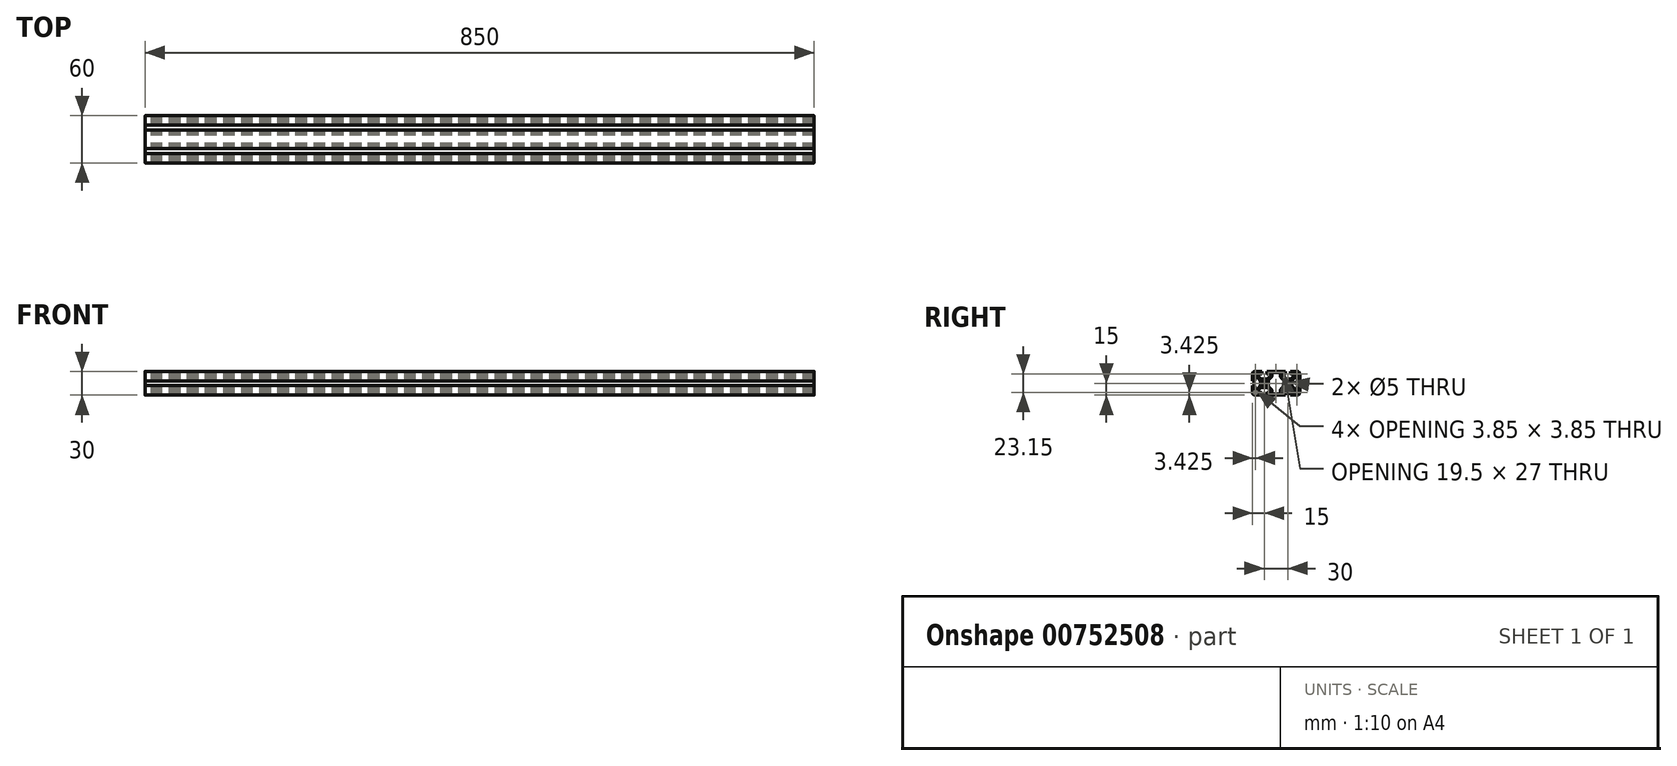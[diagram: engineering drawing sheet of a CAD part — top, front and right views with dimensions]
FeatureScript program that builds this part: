
annotation { "Feature Type Name" : "Feature", "Feature Type Description" : "" }
export const myFeature = defineFeature(function(context is Context, id is Id, definition is map)
    precondition{}
    {
        {
            var Q0;
            Q0=qCreatedBy(makeId("Right.planeOp"),FACE);
            var sketch = newSketch(context, id + "F0", { "sketchPlane" : qUnion([Q0])});
            skLineSegment(sketch, "E0.bottom", {"start": v(-12, 15) * mm, "end": v(-3.1, 15) * mm});
            skLineSegment(sketch, "E0.top", {"start": v(-12, -15) * mm, "end": v(-3.1, -15) * mm});
            skLineSegment(sketch, "E1", {"start": v(0, 31.7) * mm, "end": v(0, -24.01) * mm, "construction": true});
            skLineSegment(sketch, "E2", {"start": v(-29.71, 0) * mm, "end": v(21.95, 0) * mm, "construction": true});
            skLineSegment(sketch, "E3", {"start": v(-3.1, 15) * mm, "end": v(-3.1, 12.8) * mm});
            skLineSegment(sketch, "E4", {"start": v(-3.9, 12) * mm, "end": v(-5.6, 12) * mm});
            skLineSegment(sketch, "E5", {"start": v(-5.6, 12) * mm, "end": v(-5.6, 13.5) * mm});
            skLineSegment(sketch, "E6", {"start": v(-5.6, 13.5) * mm, "end": v(-8.15, 13.5) * mm});
            skLineSegment(sketch, "E7", {"start": v(-8.15, 13.5) * mm, "end": v(-8.15, 10.8) * mm});
            skLineSegment(sketch, "E8", {"start": v(-7.27, 8.68) * mm, "end": v(-4.72, 6.13) * mm});
            skLineSegment(sketch, "E9", {"start": v(-2.6, 5.25) * mm, "end": v(2.6, 5.25) * mm});
            skLineSegment(sketch, "E10", {"start": v(4.72, 6.13) * mm, "end": v(7.27, 8.68) * mm});
            skLineSegment(sketch, "E11", {"start": v(8.15, 10.8) * mm, "end": v(8.15, 13.5) * mm});
            skLineSegment(sketch, "E12", {"start": v(8.15, 13.5) * mm, "end": v(5.6, 13.5) * mm});
            skLineSegment(sketch, "E13", {"start": v(5.6, 13.5) * mm, "end": v(5.6, 12) * mm});
            skLineSegment(sketch, "E14", {"start": v(5.6, 12) * mm, "end": v(3.9, 12) * mm});
            skLineSegment(sketch, "E15", {"start": v(3.1, 12.8) * mm, "end": v(3.1, 15) * mm});
            skLineSegment(sketch, "E16.trimOffspring", {"start": v(3.1, 15) * mm, "end": v(12, 15) * mm});
            skLineSegment(sketch, "E17.bottom", {"start": v(-12, 13.5) * mm, "end": v(-9.65, 13.5) * mm});
            skLineSegment(sketch, "E17.top", {"start": v(-13.5, 9.65) * mm, "end": v(-9.65, 9.65) * mm});
            skLineSegment(sketch, "E17.left", {"start": v(-13.5, 12) * mm, "end": v(-13.5, 9.65) * mm});
            skLineSegment(sketch, "E17.right", {"start": v(-9.65, 13.5) * mm, "end": v(-9.65, 9.65) * mm});
            skPoint(sketch, "E18.visualSharp", {"position": v(-13.5, 13.5) * mm});
            skArc(sketch, "E18.filletArc", {"start": v(-12, 13.5) * mm, "mid": v(-13.06, 13.06) * mm, "end": v(-13.5, 12) * mm});
            skPoint(sketch, "E19.visualSharp", {"position": v(-14.85, 15) * mm});
            skArc(sketch, "E19.filletArc", {"start": v(-12, 15) * mm, "mid": v(-14.12, 14.12) * mm, "end": v(-15, 12) * mm});
            skPoint(sketch, "E20.visualSharp", {"position": v(-14.85, -15) * mm});
            skArc(sketch, "E20.filletArc", {"start": v(-15, -12) * mm, "mid": v(-14.12, -14.12) * mm, "end": v(-12, -15) * mm});
            skPoint(sketch, "E21.visualSharp", {"position": v(15.15, -15) * mm});
            skPoint(sketch, "E22.visualSharp", {"position": v(-8.15, 9.56) * mm});
            skArc(sketch, "E22.filletArc", {"start": v(-8.15, 10.8) * mm, "mid": v(-7.92, 9.66) * mm, "end": v(-7.27, 8.68) * mm});
            skPoint(sketch, "E23.visualSharp", {"position": v(-3.84, 5.25) * mm});
            skArc(sketch, "E23.filletArc", {"start": v(-4.72, 6.13) * mm, "mid": v(-3.74, 5.48) * mm, "end": v(-2.6, 5.25) * mm});
            skPoint(sketch, "E24.visualSharp", {"position": v(3.84, 5.25) * mm});
            skArc(sketch, "E24.filletArc", {"start": v(2.6, 5.25) * mm, "mid": v(3.74, 5.48) * mm, "end": v(4.72, 6.13) * mm});
            skPoint(sketch, "E25.visualSharp", {"position": v(8.15, 9.56) * mm});
            skArc(sketch, "E25.filletArc", {"start": v(7.27, 8.68) * mm, "mid": v(7.92, 9.66) * mm, "end": v(8.15, 10.8) * mm});
            skPoint(sketch, "E26.visualSharp", {"position": v(3.1, 12) * mm});
            skArc(sketch, "E26.filletArc", {"start": v(3.1, 12.8) * mm, "mid": v(3.33, 12.23) * mm, "end": v(3.9, 12) * mm});
            skPoint(sketch, "E27.visualSharp", {"position": v(-3.1, 12) * mm});
            skArc(sketch, "E27.filletArc", {"start": v(-3.9, 12) * mm, "mid": v(-3.33, 12.23) * mm, "end": v(-3.1, 12.8) * mm});
            skLineSegment(sketch, "E28.1.0", {"start": v(-5.25, -2.6) * mm, "end": v(-5.25, 2.6) * mm});
            skLineSegment(sketch, "E28.1.1", {"start": v(-12.8, 3.1) * mm, "end": v(-15, 3.1) * mm});
            skLineSegment(sketch, "E28.1.2", {"start": v(-6.13, 4.72) * mm, "end": v(-8.68, 7.27) * mm});
            skPoint(sketch, "E28.1.3", {"position": v(-12, -3.1) * mm});
            skLineSegment(sketch, "E28.1.4", {"start": v(-13.5, -5.6) * mm, "end": v(-13.5, -8.15) * mm});
            skPoint(sketch, "E28.1.5", {"position": v(-5.25, 3.84) * mm});
            skLineSegment(sketch, "E28.1.6", {"start": v(-13.5, -12) * mm, "end": v(-13.5, -9.65) * mm});
            skPoint(sketch, "E28.1.7", {"position": v(-5.25, -3.84) * mm});
            skLineSegment(sketch, "E28.1.8", {"start": v(-10.8, 8.15) * mm, "end": v(-13.5, 8.15) * mm});
            skLineSegment(sketch, "E28.1.9", {"start": v(-9.65, -13.5) * mm, "end": v(-9.65, -9.65) * mm});
            skLineSegment(sketch, "E28.1.10", {"start": v(-12, -13.5) * mm, "end": v(-9.65, -13.5) * mm});
            skLineSegment(sketch, "E28.1.11", {"start": v(-13.5, -8.15) * mm, "end": v(-10.8, -8.15) * mm});
            skLineSegment(sketch, "E28.1.12", {"start": v(-13.5, -9.65) * mm, "end": v(-9.65, -9.65) * mm});
            skPoint(sketch, "E28.1.13", {"position": v(-9.56, 8.15) * mm});
            skLineSegment(sketch, "E28.1.14", {"start": v(-8.68, -7.27) * mm, "end": v(-6.13, -4.72) * mm});
            skPoint(sketch, "E28.1.15", {"position": v(-12, 3.1) * mm});
            skPoint(sketch, "E28.1.16", {"position": v(-9.56, -8.15) * mm});
            skLineSegment(sketch, "E28.1.17", {"start": v(-15, -3.1) * mm, "end": v(-12.8, -3.1) * mm});
            skLineSegment(sketch, "E28.1.18", {"start": v(-13.5, 8.15) * mm, "end": v(-13.5, 5.6) * mm});
            skArc(sketch, "E28.1.19", {"start": v(-10.8, -8.15) * mm, "mid": v(-9.66, -7.92) * mm, "end": v(-8.68, -7.27) * mm});
            skArc(sketch, "E28.1.20", {"start": v(-6.13, -4.72) * mm, "mid": v(-5.48, -3.74) * mm, "end": v(-5.25, -2.6) * mm});
            skArc(sketch, "E28.1.21", {"start": v(-13.5, -12) * mm, "mid": v(-13.06, -13.06) * mm, "end": v(-12, -13.5) * mm});
            skArc(sketch, "E28.1.22", {"start": v(-8.68, 7.27) * mm, "mid": v(-9.66, 7.92) * mm, "end": v(-10.8, 8.15) * mm});
            skArc(sketch, "E28.1.23", {"start": v(-5.25, 2.6) * mm, "mid": v(-5.48, 3.74) * mm, "end": v(-6.13, 4.72) * mm});
            skLineSegment(sketch, "E28.1.24", {"start": v(-12, -5.6) * mm, "end": v(-13.5, -5.6) * mm});
            skLineSegment(sketch, "E28.1.25", {"start": v(-13.5, 5.6) * mm, "end": v(-12, 5.6) * mm});
            skLineSegment(sketch, "E28.1.26", {"start": v(-12, 5.6) * mm, "end": v(-12, 3.9) * mm});
            skLineSegment(sketch, "E28.1.27", {"start": v(-12, -3.9) * mm, "end": v(-12, -5.6) * mm});
            skArc(sketch, "E28.1.28", {"start": v(-12, -3.9) * mm, "mid": v(-12.23, -3.33) * mm, "end": v(-12.8, -3.1) * mm});
            skArc(sketch, "E28.1.29", {"start": v(-12.8, 3.1) * mm, "mid": v(-12.23, 3.33) * mm, "end": v(-12, 3.9) * mm});
            skLineSegment(sketch, "E28.2.0", {"start": v(2.6, -5.25) * mm, "end": v(-2.6, -5.25) * mm});
            skLineSegment(sketch, "E28.2.1", {"start": v(-3.1, -12.8) * mm, "end": v(-3.1, -15) * mm});
            skLineSegment(sketch, "E28.2.2", {"start": v(-4.72, -6.13) * mm, "end": v(-7.27, -8.68) * mm});
            skPoint(sketch, "E28.2.3", {"position": v(3.1, -12) * mm});
            skLineSegment(sketch, "E28.2.4", {"start": v(5.6, -13.5) * mm, "end": v(8.15, -13.5) * mm});
            skPoint(sketch, "E28.2.5", {"position": v(-3.84, -5.25) * mm});
            skPoint(sketch, "E28.2.7", {"position": v(3.84, -5.25) * mm});
            skLineSegment(sketch, "E28.2.8", {"start": v(-8.15, -10.8) * mm, "end": v(-8.15, -13.5) * mm});
            skLineSegment(sketch, "E28.2.11", {"start": v(8.15, -13.5) * mm, "end": v(8.15, -10.8) * mm});
            skLineSegment(sketch, "E28.2.12", {"start": v(9.65, -13.5) * mm, "end": v(9.65, -9.65) * mm});
            skPoint(sketch, "E28.2.13", {"position": v(-8.15, -9.56) * mm});
            skLineSegment(sketch, "E28.2.14", {"start": v(7.27, -8.68) * mm, "end": v(4.72, -6.13) * mm});
            skPoint(sketch, "E28.2.15", {"position": v(-3.1, -12) * mm});
            skPoint(sketch, "E28.2.16", {"position": v(8.15, -9.56) * mm});
            skLineSegment(sketch, "E28.2.17", {"start": v(3.1, -15) * mm, "end": v(3.1, -12.8) * mm});
            skLineSegment(sketch, "E28.2.18", {"start": v(-8.15, -13.5) * mm, "end": v(-5.6, -13.5) * mm});
            skArc(sketch, "E28.2.19", {"start": v(8.15, -10.8) * mm, "mid": v(7.92, -9.66) * mm, "end": v(7.27, -8.68) * mm});
            skArc(sketch, "E28.2.20", {"start": v(4.72, -6.13) * mm, "mid": v(3.74, -5.48) * mm, "end": v(2.6, -5.25) * mm});
            skArc(sketch, "E28.2.22", {"start": v(-7.27, -8.68) * mm, "mid": v(-7.92, -9.66) * mm, "end": v(-8.15, -10.8) * mm});
            skArc(sketch, "E28.2.23", {"start": v(-2.6, -5.25) * mm, "mid": v(-3.74, -5.48) * mm, "end": v(-4.72, -6.13) * mm});
            skLineSegment(sketch, "E28.2.24", {"start": v(5.6, -12) * mm, "end": v(5.6, -13.5) * mm});
            skLineSegment(sketch, "E28.2.25", {"start": v(-5.6, -13.5) * mm, "end": v(-5.6, -12) * mm});
            skLineSegment(sketch, "E28.2.26", {"start": v(-5.6, -12) * mm, "end": v(-3.9, -12) * mm});
            skLineSegment(sketch, "E28.2.27", {"start": v(3.9, -12) * mm, "end": v(5.6, -12) * mm});
            skArc(sketch, "E28.2.28", {"start": v(3.9, -12) * mm, "mid": v(3.33, -12.23) * mm, "end": v(3.1, -12.8) * mm});
            skArc(sketch, "E28.2.29", {"start": v(-3.1, -12.8) * mm, "mid": v(-3.33, -12.23) * mm, "end": v(-3.9, -12) * mm});
            skLineSegment(sketch, "E28.3.0", {"start": v(5.25, 2.6) * mm, "end": v(5.25, -2.6) * mm});
            skLineSegment(sketch, "E28.3.2", {"start": v(6.13, -4.72) * mm, "end": v(8.68, -7.27) * mm});
            skPoint(sketch, "E28.3.5", {"position": v(5.25, -3.84) * mm});
            skPoint(sketch, "E28.3.7", {"position": v(5.25, 3.84) * mm});
            skLineSegment(sketch, "E28.3.9", {"start": v(9.65, 13.5) * mm, "end": v(9.65, 9.56) * mm});
            skPoint(sketch, "E28.3.13", {"position": v(9.56, -8.15) * mm});
            skLineSegment(sketch, "E28.3.14", {"start": v(8.71, 7.3) * mm, "end": v(6.13, 4.72) * mm});
            skPoint(sketch, "E28.3.16", {"position": v(9.56, 8.15) * mm});
            skArc(sketch, "E28.3.20", {"start": v(6.13, 4.72) * mm, "mid": v(5.48, 3.74) * mm, "end": v(5.25, 2.6) * mm});
            skArc(sketch, "E28.3.23", {"start": v(5.25, -2.6) * mm, "mid": v(5.48, -3.74) * mm, "end": v(6.13, -4.72) * mm});
            skPoint(sketch, "E28.center", {"position": v(0, 0) * mm});
            skLineSegment(sketch, "E29.trimOffspring", {"start": v(-15, -3.1) * mm, "end": v(-15, -12) * mm});
            skLineSegment(sketch, "E30.trimOffspring", {"start": v(3.1, -15) * mm, "end": v(12, -15) * mm});
            skLineSegment(sketch, "E31", {"start": v(-15, 12) * mm, "end": v(-15, 3.1) * mm});
            skCircle(sketch, "E32", {"center": v(0, 0) * mm, "radius": 2.5 * mm});
            skPoint(sketch, "E33.1.0.0", {"position": v(26.9, -12) * mm});
            skPoint(sketch, "E33.1.0.1", {"position": v(45.65, 15) * mm});
            skPoint(sketch, "E33.1.0.3", {"position": v(30, 0) * mm});
            skPoint(sketch, "E33.1.0.4", {"position": v(35.25, -3.84) * mm});
            skPoint(sketch, "E33.1.0.5", {"position": v(33.1, 12) * mm});
            skPoint(sketch, "E33.1.0.7", {"position": v(35.25, 3.84) * mm});
            skPoint(sketch, "E33.1.0.8", {"position": v(42, 3.1) * mm});
            skPoint(sketch, "E33.1.0.9", {"position": v(33.1, -12) * mm});
            skLineSegment(sketch, "E33.1.0.10", {"start": v(30, 31.7) * mm, "end": v(30, -24.01) * mm, "construction": true});
            skLineSegment(sketch, "E33.1.0.11", {"start": v(0.29, 0) * mm, "end": v(51.95, 0) * mm, "construction": true});
            skPoint(sketch, "E33.1.0.13", {"position": v(42.5, -2.6) * mm});
            skPoint(sketch, "E33.1.0.15", {"position": v(45.15, -15) * mm});
            skPoint(sketch, "E33.1.0.16", {"position": v(24.75, 3.84) * mm});
            skPoint(sketch, "E33.1.0.17", {"position": v(24.75, -3.84) * mm});
            skPoint(sketch, "E33.1.0.18", {"position": v(26.16, 5.25) * mm});
            skLineSegment(sketch, "E33.1.0.20", {"start": v(32.6, -5.25) * mm, "end": v(27.4, -5.25) * mm});
            skArc(sketch, "E33.1.0.21", {"start": v(42, -15) * mm, "mid": v(44.12, -14.12) * mm, "end": v(45, -12) * mm});
            skPoint(sketch, "E33.1.0.22", {"position": v(33.84, 5.25) * mm});
            skArc(sketch, "E33.1.0.23", {"start": v(45, 12) * mm, "mid": v(44.12, 14.12) * mm, "end": v(42, 15) * mm});
            skCircle(sketch, "E33.1.0.24", {"center": v(30, 0) * mm, "radius": 2.5 * mm});
            skLineSegment(sketch, "E33.1.0.26", {"start": v(27.4, 5.25) * mm, "end": v(32.6, 5.25) * mm});
            skPoint(sketch, "E33.1.0.27", {"position": v(26.16, -5.25) * mm});
            skPoint(sketch, "E33.1.0.28", {"position": v(33.84, -5.25) * mm});
            skLineSegment(sketch, "E33.1.0.29", {"start": v(35.25, 2.6) * mm, "end": v(35.25, -2.6) * mm});
            skLineSegment(sketch, "E33.1.0.30", {"start": v(24.75, -2.6) * mm, "end": v(24.75, 2.6) * mm});
            skLineSegment(sketch, "E33.1.0.31", {"start": v(42.85, -3.1) * mm, "end": v(45, -3.1) * mm});
            skArc(sketch, "E33.1.0.32", {"start": v(24.75, 2.6) * mm, "mid": v(24.52, 3.74) * mm, "end": v(23.87, 4.72) * mm});
            skArc(sketch, "E33.1.0.34", {"start": v(35.25, -2.6) * mm, "mid": v(35.48, -3.74) * mm, "end": v(36.13, -4.72) * mm});
            skPoint(sketch, "E33.1.0.35", {"position": v(38.15, -9.56) * mm});
            skLineSegment(sketch, "E33.1.0.36", {"start": v(36.13, -4.72) * mm, "end": v(38.68, -7.27) * mm});
            skLineSegment(sketch, "E33.1.0.37", {"start": v(37.27, -8.68) * mm, "end": v(34.72, -6.13) * mm});
            skLineSegment(sketch, "E33.1.0.39", {"start": v(23.87, 4.72) * mm, "end": v(21.32, 7.27) * mm});
            skPoint(sketch, "E33.1.0.40", {"position": v(20.44, 8.15) * mm});
            skLineSegment(sketch, "E33.1.0.41", {"start": v(33.1, -15) * mm, "end": v(33.1, -12.8) * mm});
            skLineSegment(sketch, "E33.1.0.43", {"start": v(43.5, -5.6) * mm, "end": v(42.05, -5.6) * mm});
            skPoint(sketch, "E33.1.0.44", {"position": v(21.85, 9.56) * mm});
            skLineSegment(sketch, "E33.1.0.45", {"start": v(21.85, -13.5) * mm, "end": v(24.4, -13.5) * mm});
            skLineSegment(sketch, "E33.1.0.46", {"start": v(42.05, -5.6) * mm, "end": v(42.05, -3.9) * mm});
            skPoint(sketch, "E33.1.0.47", {"position": v(20.44, -8.15) * mm});
            skArc(sketch, "E33.1.0.52", {"start": v(42.85, -3.1) * mm, "mid": v(42.29, -3.33) * mm, "end": v(42.05, -3.9) * mm});
            skLineSegment(sketch, "E33.1.0.54", {"start": v(26.9, -12.8) * mm, "end": v(26.9, -15) * mm});
            skLineSegment(sketch, "E33.1.0.55", {"start": v(45, -3.1) * mm, "end": v(45, -12) * mm});
            skArc(sketch, "E33.1.0.56", {"start": v(27.4, -5.25) * mm, "mid": v(26.26, -5.48) * mm, "end": v(25.28, -6.13) * mm});
            skLineSegment(sketch, "E33.1.0.57", {"start": v(24.4, -13.5) * mm, "end": v(24.4, -12) * mm});
            skArc(sketch, "E33.1.0.59", {"start": v(25.28, 6.13) * mm, "mid": v(26.26, 5.48) * mm, "end": v(27.4, 5.25) * mm});
            skLineSegment(sketch, "E33.1.0.61", {"start": v(25.28, -6.13) * mm, "end": v(22.73, -8.68) * mm});
            skLineSegment(sketch, "E33.1.0.62", {"start": v(21.32, -7.27) * mm, "end": v(23.87, -4.72) * mm});
            skLineSegment(sketch, "E33.1.0.63", {"start": v(33.1, -15) * mm, "end": v(42, -15) * mm});
            skLineSegment(sketch, "E33.1.0.64", {"start": v(24.4, -12) * mm, "end": v(26.1, -12) * mm});
            skArc(sketch, "E33.1.0.65", {"start": v(32.6, 5.25) * mm, "mid": v(33.74, 5.48) * mm, "end": v(34.72, 6.13) * mm});
            skLineSegment(sketch, "E33.1.0.66", {"start": v(43.5, -8.15) * mm, "end": v(43.5, -5.6) * mm});
            skPoint(sketch, "E33.1.0.67", {"position": v(38.15, 9.56) * mm});
            skPoint(sketch, "E33.1.0.68", {"position": v(39.56, -8.15) * mm});
            skLineSegment(sketch, "E33.1.0.69", {"start": v(21.85, -10.8) * mm, "end": v(21.85, -13.5) * mm});
            skLineSegment(sketch, "E33.1.0.70", {"start": v(18, -15) * mm, "end": v(26.9, -15) * mm});
            skLineSegment(sketch, "E33.1.0.71", {"start": v(45, 12) * mm, "end": v(45, 3.1) * mm});
            skLineSegment(sketch, "E33.1.0.72", {"start": v(22.73, 8.68) * mm, "end": v(25.28, 6.13) * mm});
            skArc(sketch, "E33.1.0.73", {"start": v(36.13, 4.72) * mm, "mid": v(35.48, 3.74) * mm, "end": v(35.25, 2.6) * mm});
            skPoint(sketch, "E33.1.0.74", {"position": v(26.9, 12) * mm});
            skArc(sketch, "E33.1.0.75", {"start": v(33.9, -12) * mm, "mid": v(33.33, -12.23) * mm, "end": v(33.1, -12.8) * mm});
            skArc(sketch, "E33.1.0.76", {"start": v(23.87, -4.72) * mm, "mid": v(24.52, -3.74) * mm, "end": v(24.75, -2.6) * mm});
            skPoint(sketch, "E33.1.0.77", {"position": v(39.56, 8.15) * mm});
            skArc(sketch, "E33.1.0.78", {"start": v(26.9, -12.8) * mm, "mid": v(26.67, -12.23) * mm, "end": v(26.1, -12) * mm});
            skPoint(sketch, "E33.1.0.79", {"position": v(21.85, -9.56) * mm});
            skLineSegment(sketch, "E33.1.0.80", {"start": v(33.1, 15) * mm, "end": v(42, 15) * mm});
            skLineSegment(sketch, "E33.1.0.82", {"start": v(39.65, -13.5) * mm, "end": v(39.65, -9.65) * mm});
            skLineSegment(sketch, "E33.1.0.84", {"start": v(42, 5.6) * mm, "end": v(43.5, 5.6) * mm});
            skLineSegment(sketch, "E33.1.0.85", {"start": v(43.5, 5.6) * mm, "end": v(43.5, 8.15) * mm});
            skLineSegment(sketch, "E33.1.0.87", {"start": v(20.35, 13.5) * mm, "end": v(20.35, 9.65) * mm});
            skLineSegment(sketch, "E33.1.0.88", {"start": v(43.5, 12) * mm, "end": v(43.5, 9.65) * mm});
            skLineSegment(sketch, "E33.1.0.93", {"start": v(42, 3.9) * mm, "end": v(42, 5.6) * mm});
            skLineSegment(sketch, "E33.1.0.94", {"start": v(40.8, -8.15) * mm, "end": v(43.5, -8.15) * mm});
            skArc(sketch, "E33.1.0.95", {"start": v(38.15, -10.8) * mm, "mid": v(37.92, -9.66) * mm, "end": v(37.27, -8.68) * mm});
            skLineSegment(sketch, "E33.1.0.96", {"start": v(20.35, -13.5) * mm, "end": v(20.35, -9.65) * mm});
            skArc(sketch, "E33.1.0.97", {"start": v(42, 3.9) * mm, "mid": v(42.23, 3.33) * mm, "end": v(42.8, 3.1) * mm});
            skLineSegment(sketch, "E33.1.0.98", {"start": v(39.65, 13.5) * mm, "end": v(39.65, 9.65) * mm});
            skArc(sketch, "E33.1.0.99", {"start": v(34.72, -6.13) * mm, "mid": v(33.74, -5.48) * mm, "end": v(32.6, -5.25) * mm});
            skLineSegment(sketch, "E33.1.0.101", {"start": v(42, 13.5) * mm, "end": v(39.65, 13.5) * mm});
            skArc(sketch, "E33.1.0.102", {"start": v(42, -13.5) * mm, "mid": v(43.06, -13.06) * mm, "end": v(43.5, -12) * mm});
            skLineSegment(sketch, "E33.1.0.104", {"start": v(43.5, 8.15) * mm, "end": v(40.76, 8.15) * mm});
            skArc(sketch, "E33.1.0.105", {"start": v(22.73, -8.68) * mm, "mid": v(22.08, -9.66) * mm, "end": v(21.85, -10.8) * mm});
            skLineSegment(sketch, "E33.1.0.107", {"start": v(43.5, 9.65) * mm, "end": v(39.65, 9.65) * mm});
            skLineSegment(sketch, "E33.1.0.108", {"start": v(35.6, -13.5) * mm, "end": v(38.15, -13.5) * mm});
            skLineSegment(sketch, "E33.1.0.109", {"start": v(45, 3.1) * mm, "end": v(42.8, 3.1) * mm});
            skArc(sketch, "E33.1.0.110", {"start": v(21.85, 10.8) * mm, "mid": v(22.08, 9.66) * mm, "end": v(22.73, 8.68) * mm});
            skLineSegment(sketch, "E33.1.0.111", {"start": v(38.68, 7.27) * mm, "end": v(36.13, 4.72) * mm});
            skLineSegment(sketch, "E33.1.0.112", {"start": v(35.6, -12) * mm, "end": v(35.6, -13.5) * mm});
            skLineSegment(sketch, "E33.1.0.113", {"start": v(42, -13.5) * mm, "end": v(39.65, -13.5) * mm});
            skLineSegment(sketch, "E33.1.0.115", {"start": v(33.9, -12) * mm, "end": v(35.6, -12) * mm});
            skArc(sketch, "E33.1.0.117", {"start": v(37.27, 8.68) * mm, "mid": v(37.92, 9.66) * mm, "end": v(38.15, 10.8) * mm});
            skArc(sketch, "E33.1.0.118", {"start": v(40.76, 8.15) * mm, "mid": v(39.64, 7.91) * mm, "end": v(38.68, 7.27) * mm});
            skLineSegment(sketch, "E33.1.0.119", {"start": v(38.15, 10.8) * mm, "end": v(38.15, 13.5) * mm});
            skLineSegment(sketch, "E33.1.0.120", {"start": v(38.15, 13.5) * mm, "end": v(35.6, 13.5) * mm});
            skLineSegment(sketch, "E33.1.0.121", {"start": v(35.6, 13.5) * mm, "end": v(35.6, 12) * mm});
            skLineSegment(sketch, "E33.1.0.122", {"start": v(18, 15) * mm, "end": v(26.9, 15) * mm});
            skLineSegment(sketch, "E33.1.0.123", {"start": v(26.9, 15) * mm, "end": v(26.9, 12.8) * mm});
            skLineSegment(sketch, "E33.1.0.124", {"start": v(24.4, 12) * mm, "end": v(24.4, 13.5) * mm});
            skLineSegment(sketch, "E33.1.0.125", {"start": v(24.4, 13.5) * mm, "end": v(21.85, 13.5) * mm});
            skLineSegment(sketch, "E33.1.0.126", {"start": v(21.85, 13.5) * mm, "end": v(21.85, 10.8) * mm});
            skLineSegment(sketch, "E33.1.0.127", {"start": v(34.72, 6.13) * mm, "end": v(37.27, 8.68) * mm});
            skLineSegment(sketch, "E33.1.0.128", {"start": v(35.6, 12) * mm, "end": v(33.9, 12) * mm});
            skLineSegment(sketch, "E33.1.0.129", {"start": v(43.5, -9.65) * mm, "end": v(39.65, -9.65) * mm});
            skLineSegment(sketch, "E33.1.0.130", {"start": v(33.1, 12.8) * mm, "end": v(33.1, 15) * mm});
            skLineSegment(sketch, "E33.1.0.131", {"start": v(43.5, -12) * mm, "end": v(43.5, -9.65) * mm});
            skArc(sketch, "E33.1.0.133", {"start": v(43.5, 12) * mm, "mid": v(43.06, 13.06) * mm, "end": v(42, 13.5) * mm});
            skLineSegment(sketch, "E33.1.0.134", {"start": v(38.15, -13.5) * mm, "end": v(38.15, -10.8) * mm});
            skArc(sketch, "E33.1.0.136", {"start": v(38.68, -7.27) * mm, "mid": v(39.66, -7.92) * mm, "end": v(40.8, -8.15) * mm});
            skLineSegment(sketch, "E33.1.0.138", {"start": v(26.1, 12) * mm, "end": v(24.4, 12) * mm});
            skArc(sketch, "E33.1.0.139", {"start": v(33.1, 12.8) * mm, "mid": v(33.33, 12.23) * mm, "end": v(33.9, 12) * mm});
            skArc(sketch, "E33.1.0.140", {"start": v(26.1, 12) * mm, "mid": v(26.67, 12.23) * mm, "end": v(26.9, 12.8) * mm});
            skLineSegment(sketch, "E33.direction1", {"start": v(-14.85, -15) * mm, "end": v(15.15, -15) * mm, "construction": true});
            skLineSegment(sketch, "E34", {"start": v(9.65, 13.5) * mm, "end": v(20.35, 13.5) * mm});
            skArc(sketch, "E35", {"start": v(8.71, 7.3) * mm, "mid": v(9.4, 8.34) * mm, "end": v(9.65, 9.56) * mm});
            skArc(sketch, "E36", {"start": v(20.35, 9.65) * mm, "mid": v(20.6, 8.37) * mm, "end": v(21.32, 7.27) * mm});
            skArc(sketch, "E37", {"start": v(9.65, -9.65) * mm, "mid": v(9.4, -8.36) * mm, "end": v(8.68, -7.27) * mm});
            skArc(sketch, "E38", {"start": v(21.32, -7.27) * mm, "mid": v(20.6, -8.37) * mm, "end": v(20.35, -9.65) * mm});
            skLineSegment(sketch, "E39", {"start": v(12, -15) * mm, "end": v(18, -15) * mm});
            skLineSegment(sketch, "E40", {"start": v(12, 15) * mm, "end": v(18.49, 15) * mm});
            skLineSegment(sketch, "E41", {"start": v(9.65, -13.5) * mm, "end": v(20.35, -13.5) * mm});
            skSolve(sketch);
        }
        {
            var Q0;
            Q0=qSketchRegion(id+"F0",true);
            extrude(context, id + "F1", {"entities" : qUnion([Q0]), "depth" : 850 * mm, "offsetDistance" : 25 * mm});
        }
    });
